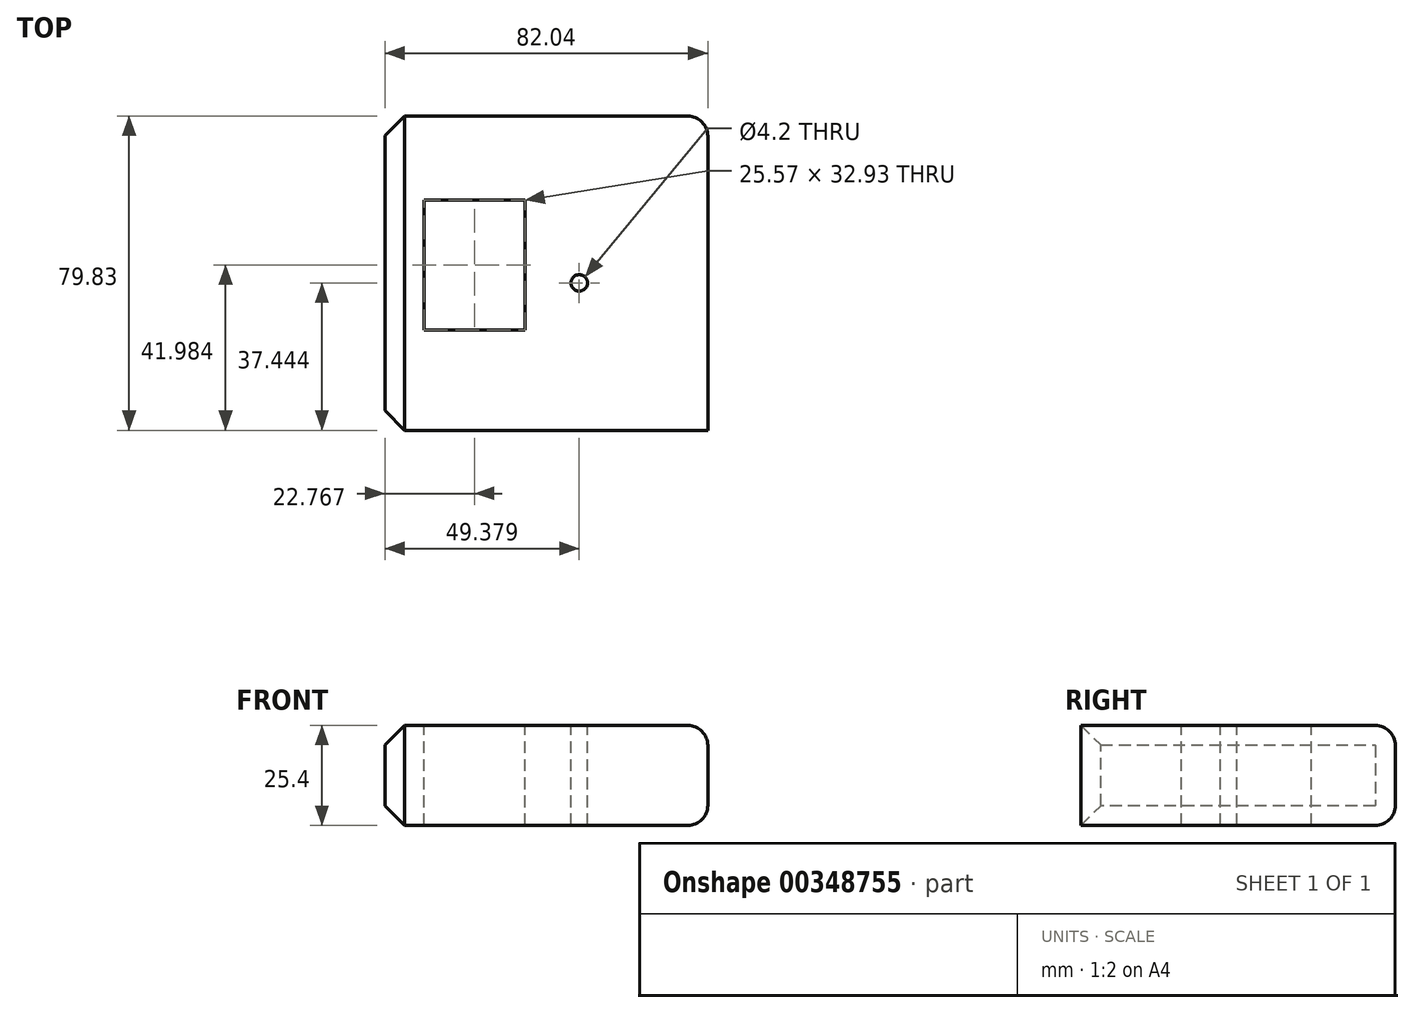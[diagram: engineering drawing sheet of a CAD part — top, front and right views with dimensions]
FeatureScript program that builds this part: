
annotation { "Feature Type Name" : "Feature", "Feature Type Description" : "" }
export const myFeature = defineFeature(function(context is Context, id is Id, definition is map)
    precondition{}
    {
        {
            var Q0;
            Q0=qCreatedBy(makeId("Top.planeOp"),FACE);
            var sketch = newSketch(context, id + "F0", { "sketchPlane" : qUnion([Q0])});
            skLineSegment(sketch, "E0.bottom", {"start": v(0, 0) * mm, "end": v(82.04, 0) * mm});
            skLineSegment(sketch, "E0.top", {"start": v(0, 79.83) * mm, "end": v(82.04, 79.83) * mm});
            skLineSegment(sketch, "E0.left", {"start": v(0, 0) * mm, "end": v(0, 79.83) * mm});
            skLineSegment(sketch, "E0.right", {"start": v(82.04, 0) * mm, "end": v(82.04, 79.83) * mm});
            skSolve(sketch);
        }
        {
            var Q0;
            Q0=makeQuery(id+"F0.imprint","IMPRINT",FACE,{"disambiguationData":[TD([[makeQuery(id+"F0.imprint","IMPRINT",EDGE,{"derivedFrom":sQuery(id+"F0.wireOp",EDGE,"E0.bottom")}),1.0]])]});
            extrude(context, id + "F1", {"entities" : qUnion([Q0]), "depth" : 25.4 * mm});
        }
        {
            var Q0;
            Q0=makeQuery(id+"F1.opExtrude","CAP_FACE",FACE,{"disambiguationData":[OSD([sQuery(id+"F0.wireOp",EDGE,"E0.bottom"),sQuery(id+"F0.wireOp",EDGE,"E0.top"),sQuery(id+"F0.wireOp",EDGE,"E0.left"),sQuery(id+"F0.wireOp",EDGE,"E0.right")])],"isStart":false});
            var sketch = newSketch(context, id + "F2", { "sketchPlane" : qUnion([Q0])});
            skPoint(sketch, "E1", {"position": v(49.38, 37.44) * mm});
            skSolve(sketch);
        }
        {
            var Q0;
            Q0=sQuery(id+"F2.wireOp",VERTEX,"E1");
            var Q1;
            Q1=makeQuery(id+"F1.opExtrude","SWEPT_BODY",BODY,{"disambiguationData":[OSD([sQuery(id+"F0.wireOp",EDGE,"E0.bottom"),sQuery(id+"F0.wireOp",EDGE,"E0.top"),sQuery(id+"F0.wireOp",EDGE,"E0.left"),sQuery(id+"F0.wireOp",EDGE,"E0.right")])]});
            hole(context, id + "F3", {"style" : HoleStyle.SIMPLE, "endStyle" : HoleEndStyle.THROUGH, "standardTappedOrClearance" : lookupTablePath({ "standard" : "ISO", "engagement" : "75%", "pitch" : "0.8 mm", "size" : "M5", "type" : "Tapped" }), "standardBlindInLast" : lookupTablePath({ "standard" : "ISO", "engagement" : "75%", "pitch" : "0.8 mm", "size" : "M5", "type" : "Tapped" }), "holeDiameter" : 4.2 * mm, "showTappedDepth" : true, "isTappedThrough" : true, "tappedDepth" : 12.7 * mm, "tapClearance" : 3, "locations" : qUnion([Q0]), "scope" : qUnion([Q1]), "majorDiameter" : 5 * mm});
        }
        {
            var Q0;
            Q0=makeQuery(id+"F1.opExtrude","SWEPT_EDGE",EDGE,{"disambiguationData":[OSD([sQuery(id+"F0.wireOp",EDGE,"E0.top"),sQuery(id+"F0.wireOp",EDGE,"E0.right")])]});
            fillet(context, id + "F4", {"entities" : qUnion([Q0]), "radius" : 5.08 * mm, "tangentPropagation" : true, "allowEdgeOverflow" : false});
        }
        {
            var Q0;
            Q0=makeQuery(id+"F1.opExtrude","CAP_EDGE",EDGE,{"disambiguationData":[OSD([sQuery(id+"F0.wireOp",EDGE,"E0.right")])],"isStart":true});
            fillet(context, id + "F5", {"entities" : qUnion([Q0]), "radius" : 5.08 * mm, "tangentPropagation" : true, "allowEdgeOverflow" : false});
        }
        {
            var Q0;
            Q0=makeQuery(id+"F1.opExtrude","CAP_EDGE",EDGE,{"disambiguationData":[OSD([sQuery(id+"F0.wireOp",EDGE,"E0.top")])],"isStart":false});
            fillet(context, id + "F6", {"entities" : qUnion([Q0]), "radius" : 5.08 * mm, "tangentPropagation" : true, "allowEdgeOverflow" : false});
        }
        {
            var Q0;
            Q0=makeQuery(id+"F1.opExtrude","CAP_FACE",FACE,{"disambiguationData":[OSD([sQuery(id+"F0.wireOp",EDGE,"E0.bottom"),sQuery(id+"F0.wireOp",EDGE,"E0.top"),sQuery(id+"F0.wireOp",EDGE,"E0.left"),sQuery(id+"F0.wireOp",EDGE,"E0.right")])],"isStart":false});
            var sketch = newSketch(context, id + "F7", { "sketchPlane" : qUnion([Q0])});
            skLineSegment(sketch, "E2.bottom", {"start": v(35.55, 25.52) * mm, "end": v(9.98, 25.52) * mm});
            skLineSegment(sketch, "E2.top", {"start": v(35.55, 58.45) * mm, "end": v(9.98, 58.45) * mm});
            skLineSegment(sketch, "E2.left", {"start": v(35.55, 25.52) * mm, "end": v(35.55, 58.45) * mm});
            skLineSegment(sketch, "E2.right", {"start": v(9.98, 25.52) * mm, "end": v(9.98, 58.45) * mm});
            skSolve(sketch);
        }
        {
            var Q0;
            Q0 = qSketchRegion(id + "F7", true);
            extrude(context, id + "F8", {"entities" : qUnion([Q0]), "operationType" : NewBodyOperationType.REMOVE, "oppositeDirection" : true, "depth" : 25.4 * mm});
        }
        {
            var Q0;
            Q0=makeQuery(id+"F1.opExtrude","SWEPT_FACE",FACE,{"disambiguationData":[OSD([sQuery(id+"F0.wireOp",EDGE,"E0.left")])]});
            chamfer(context, id + "F9", {"entities" : qUnion([Q0]), "width" : 5 * mm, "tangentPropagation" : true});
        }
    });
